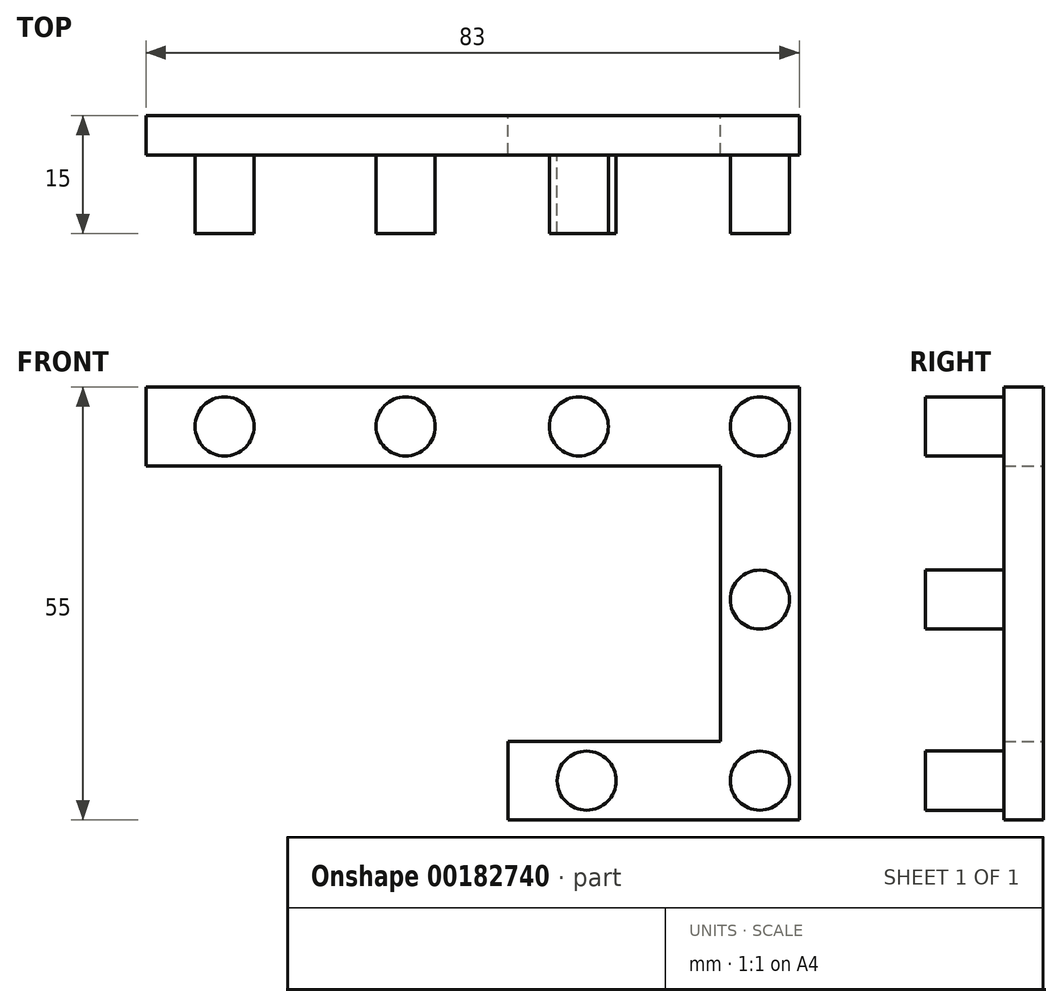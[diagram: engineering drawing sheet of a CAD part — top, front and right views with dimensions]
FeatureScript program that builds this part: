
annotation { "Feature Type Name" : "Feature", "Feature Type Description" : "" }
export const myFeature = defineFeature(function(context is Context, id is Id, definition is map)
    precondition{}
    {
        {
            var Q0;
            Q0=qCreatedBy(makeId("Front.planeOp"),FACE);
            var sketch = newSketch(context, id + "F0", { "sketchPlane" : qUnion([Q0])});
            skLineSegment(sketch, "E0", {"start": v(0, 0) * mm, "end": v(37, 0) * mm});
            skLineSegment(sketch, "E1", {"start": v(37, 0) * mm, "end": v(37, 55) * mm});
            skLineSegment(sketch, "E2", {"start": v(37, 55) * mm, "end": v(-46, 55) * mm});
            skLineSegment(sketch, "E3", {"start": v(-46, 55) * mm, "end": v(-46, 45) * mm});
            skLineSegment(sketch, "E4", {"start": v(-46, 45) * mm, "end": v(27, 45) * mm});
            skLineSegment(sketch, "E5", {"start": v(27, 45) * mm, "end": v(27, 10) * mm});
            skLineSegment(sketch, "E6", {"start": v(27, 10) * mm, "end": v(0, 10) * mm});
            skLineSegment(sketch, "E7", {"start": v(0, 10) * mm, "end": v(0, 0) * mm});
            skSolve(sketch);
        }
        {
            var Q0;
            Q0=makeQuery(id+"F0.imprint","IMPRINT",FACE,{"disambiguationData":[TD([[makeQuery(id+"F0.imprint","IMPRINT",EDGE,{"derivedFrom":sQuery(id+"F0.wireOp",EDGE,"E0")}),1.0]])]});
            extrude(context, id + "F1", {"entities" : qUnion([Q0]), "depth" : 5 * mm});
        }
        {
            var Q0;
            Q0=makeQuery(id+"F1.opExtrude","CAP_FACE",FACE,{"disambiguationData":[OSD([sQuery(id+"F0.wireOp",EDGE,"E0"),sQuery(id+"F0.wireOp",EDGE,"E1"),sQuery(id+"F0.wireOp",EDGE,"E2"),sQuery(id+"F0.wireOp",EDGE,"E3"),sQuery(id+"F0.wireOp",EDGE,"E4"),sQuery(id+"F0.wireOp",EDGE,"E5"),sQuery(id+"F0.wireOp",EDGE,"E6"),sQuery(id+"F0.wireOp",EDGE,"E7")])],"isStart":false});
            var sketch = newSketch(context, id + "F2", { "sketchPlane" : qUnion([Q0])});
            skCircle(sketch, "E8", {"center": v(-36, 50) * mm, "radius": 3.75 * mm});
            skCircle(sketch, "E9", {"center": v(-13, 50) * mm, "radius": 3.75 * mm});
            skCircle(sketch, "E10", {"center": v(9, 50) * mm, "radius": 3.75 * mm});
            skCircle(sketch, "E11", {"center": v(32, 50) * mm, "radius": 3.75 * mm});
            skCircle(sketch, "E12", {"center": v(32, 28) * mm, "radius": 3.75 * mm});
            skCircle(sketch, "E13", {"center": v(32, 5) * mm, "radius": 3.75 * mm});
            skCircle(sketch, "E14", {"center": v(10, 5) * mm, "radius": 3.75 * mm});
            skSolve(sketch);
        }
        {
            var Q0;
            Q0=makeQuery(id+"F2.imprint","IMPRINT",FACE,{"disambiguationData":[TD([[makeQuery(id+"F2.imprint","IMPRINT",EDGE,{"derivedFrom":sQuery(id+"F2.wireOp",EDGE,"E8")}),1.0]])]});
            var Q1;
            Q1=makeQuery(id+"F2.imprint","IMPRINT",FACE,{"disambiguationData":[TD([[makeQuery(id+"F2.imprint","IMPRINT",EDGE,{"derivedFrom":sQuery(id+"F2.wireOp",EDGE,"E9")}),1.0]])]});
            var Q2;
            Q2=makeQuery(id+"F2.imprint","IMPRINT",FACE,{"disambiguationData":[TD([[makeQuery(id+"F2.imprint","IMPRINT",EDGE,{"derivedFrom":sQuery(id+"F2.wireOp",EDGE,"E10")}),1.0]])]});
            var Q3;
            Q3=makeQuery(id+"F2.imprint","IMPRINT",FACE,{"disambiguationData":[TD([[makeQuery(id+"F2.imprint","IMPRINT",EDGE,{"derivedFrom":sQuery(id+"F2.wireOp",EDGE,"E11")}),1.0]])]});
            var Q4;
            Q4=makeQuery(id+"F2.imprint","IMPRINT",FACE,{"disambiguationData":[TD([[makeQuery(id+"F2.imprint","IMPRINT",EDGE,{"derivedFrom":sQuery(id+"F2.wireOp",EDGE,"E12")}),1.0]])]});
            var Q5;
            Q5=makeQuery(id+"F2.imprint","IMPRINT",FACE,{"disambiguationData":[TD([[makeQuery(id+"F2.imprint","IMPRINT",EDGE,{"derivedFrom":sQuery(id+"F2.wireOp",EDGE,"E13")}),1.0]])]});
            var Q6;
            Q6=makeQuery(id+"F2.imprint","IMPRINT",FACE,{"disambiguationData":[TD([[makeQuery(id+"F2.imprint","IMPRINT",EDGE,{"derivedFrom":sQuery(id+"F2.wireOp",EDGE,"E14")}),1.0]])]});
            extrude(context, id + "F3", {"entities" : qUnion([Q0, Q1, Q2, Q3, Q4, Q5, Q6]), "operationType" : NewBodyOperationType.ADD, "depth" : 10 * mm});
        }
    });
